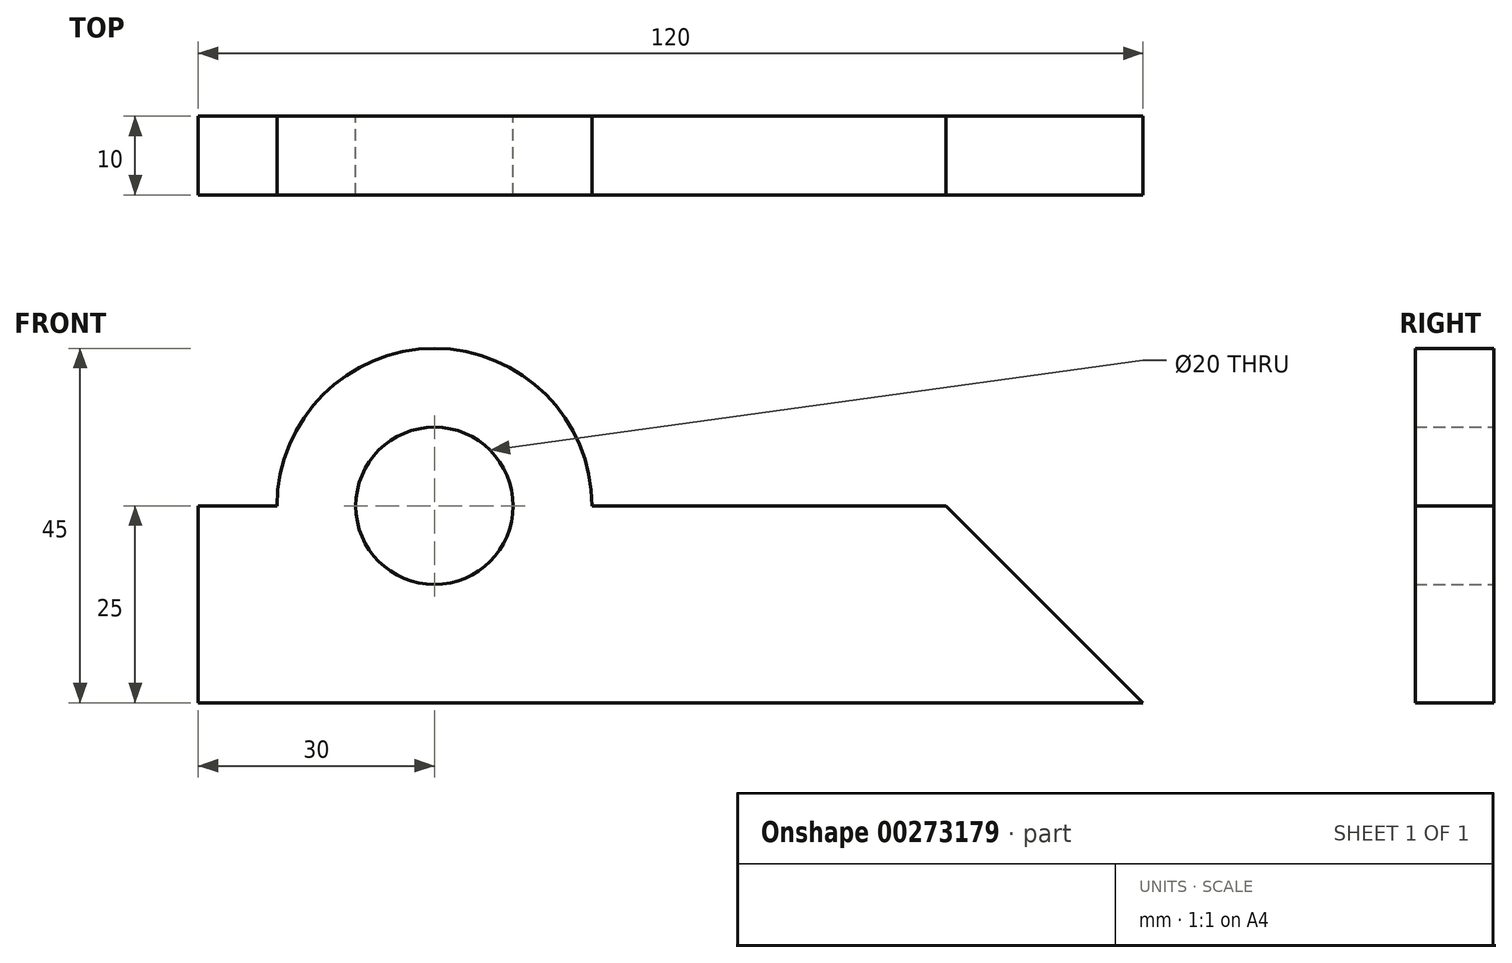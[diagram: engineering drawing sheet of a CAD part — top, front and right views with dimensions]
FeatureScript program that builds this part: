
annotation { "Feature Type Name" : "Feature", "Feature Type Description" : "" }
export const myFeature = defineFeature(function(context is Context, id is Id, definition is map)
    precondition{}
    {
        {
            var Q0;
            Q0=qCreatedBy(makeId("Front.planeOp"),FACE);
            var sketch = newSketch(context, id + "F0", { "sketchPlane" : qUnion([Q0])});
            skLineSegment(sketch, "E0", {"start": v(0, 0) * mm, "end": v(0, 25) * mm});
            skLineSegment(sketch, "E1", {"start": v(0, 25) * mm, "end": v(10, 25) * mm});
            skLineSegment(sketch, "E2", {"start": v(0, 0) * mm, "end": v(120, 0) * mm});
            skLineSegment(sketch, "E3", {"start": v(120, 0) * mm, "end": v(95, 25) * mm});
            skLineSegment(sketch, "E4", {"start": v(95, 25) * mm, "end": v(50, 25) * mm});
            skArc(sketch, "E5", {"start": v(50, 25) * mm, "mid": v(30, 45) * mm, "end": v(10, 25) * mm});
            skCircle(sketch, "E6", {"center": v(30, 25) * mm, "radius": 10 * mm});
            skSolve(sketch);
        }
        {
            var Q0;
            Q0 = qSketchRegion(id + "F0", true);
            extrude(context, id + "F1", {"entities" : qUnion([Q0]), "depth" : 10 * mm});
        }
    });
